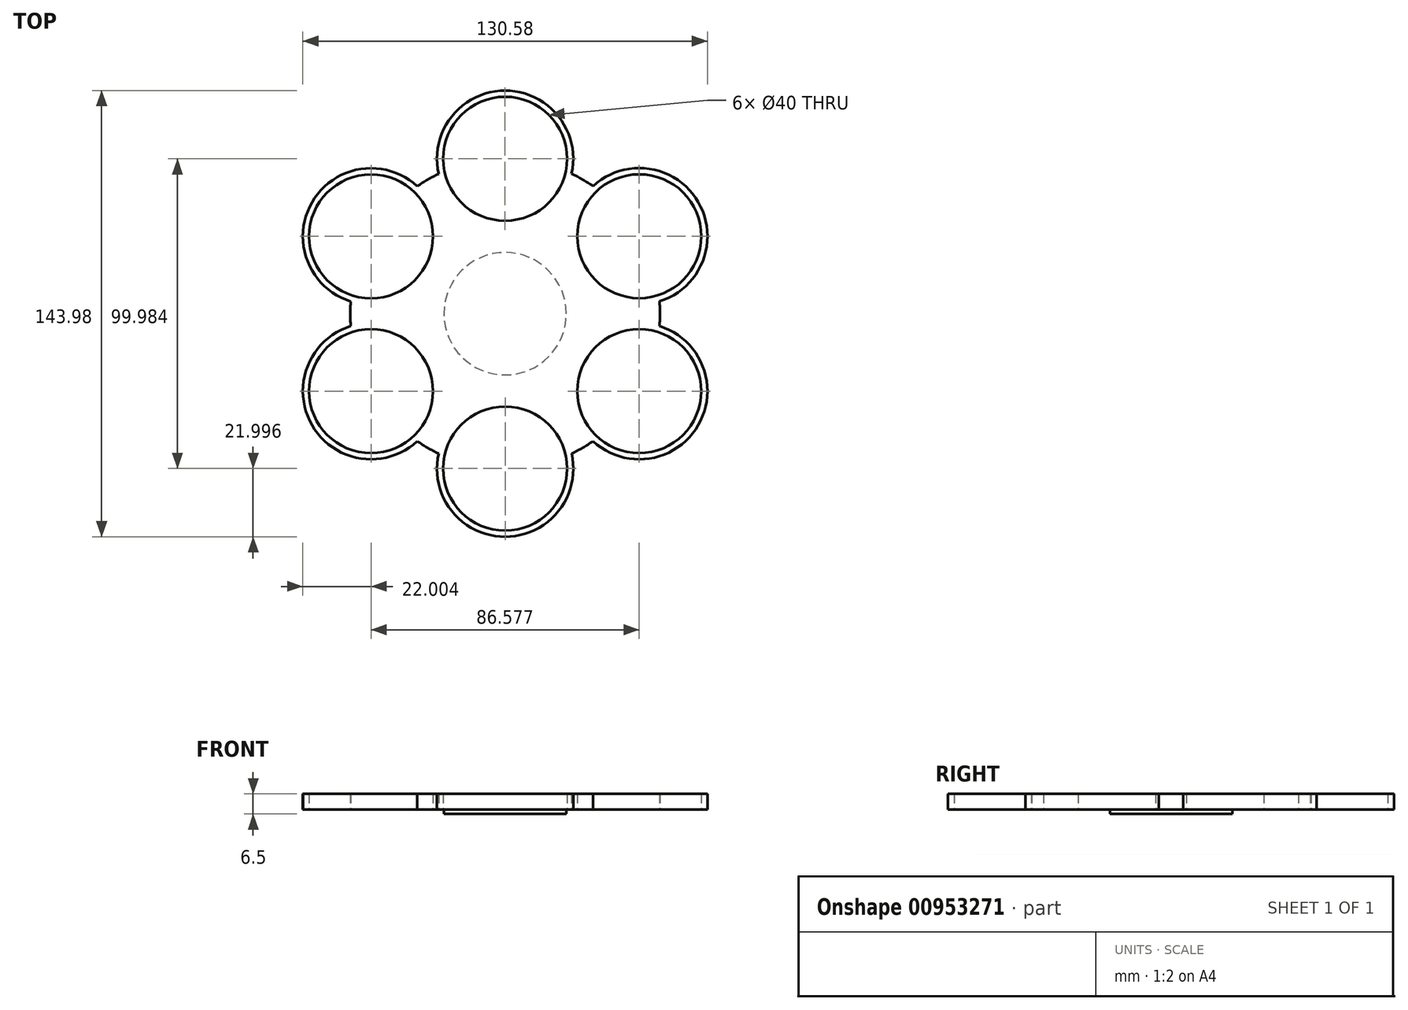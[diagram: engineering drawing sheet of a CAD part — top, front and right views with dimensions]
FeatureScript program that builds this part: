
annotation { "Feature Type Name" : "Feature", "Feature Type Description" : "" }
export const myFeature = defineFeature(function(context is Context, id is Id, definition is map)
    precondition{}
    {
        {
            var Q0;
            Q0=qCreatedBy(makeId("Top.planeOp"),FACE);
            var sketch = newSketch(context, id + "F0", { "sketchPlane" : qUnion([Q0])});
            skCircle(sketch, "E0", {"center": v(0, 0) * mm, "radius": 19.75 * mm});
            skSolve(sketch);
        }
        {
            var Q0;
            Q0=makeQuery(id+"F0.imprint","IMPRINT",FACE,{"disambiguationData":[TD([[makeQuery(id+"F0.imprint","IMPRINT",EDGE,{"derivedFrom":sQuery(id+"F0.wireOp",EDGE,"E0")}),1.0]])]});
            extrude(context, id + "F1", {"entities" : qUnion([Q0]), "depth" : 1.5 * mm, "offsetDistance" : 25 * mm});
        }
        {
            var Q0;
            Q0=makeQuery(id+"F1.opExtrude","CAP_FACE",FACE,{"disambiguationData":[OSD([sQuery(id+"F0.wireOp",EDGE,"E0")])],"isStart":false});
            var sketch = newSketch(context, id + "F2", { "sketchPlane" : qUnion([Q0])});
            skCircle(sketch, "E1", {"center": v(0, 50) * mm, "radius": 20 * mm});
            skCircle(sketch, "E2", {"center": v(43.3, 25) * mm, "radius": 20 * mm});
            skCircle(sketch, "E3", {"center": v(43.3, -25) * mm, "radius": 20 * mm});
            skCircle(sketch, "E4", {"center": v(0, -49.98) * mm, "radius": 20 * mm});
            skCircle(sketch, "E5", {"center": v(-43.27, -25) * mm, "radius": 20 * mm});
            skCircle(sketch, "E6", {"center": v(-43.28, 24.96) * mm, "radius": 20 * mm});
            skArc(sketch, "E7", {"start": v(-28.35, 41.13) * mm, "mid": v(-62.33, 35.96) * mm, "end": v(-49.81, 3.96) * mm});
            skArc(sketch, "E8", {"start": v(-49.81, -4) * mm, "mid": v(-62.33, -36) * mm, "end": v(-28.35, -41.16) * mm});
            skArc(sketch, "E9", {"start": v(-49.81, -4) * mm, "mid": v(-49.97, -0.02) * mm, "end": v(-49.81, 3.96) * mm});
            skArc(sketch, "E10", {"start": v(-21.45, -45.14) * mm, "mid": v(0, -71.98) * mm, "end": v(21.47, -45.14) * mm});
            skArc(sketch, "E11", {"start": v(28.37, -41.16) * mm, "mid": v(62.35, -36) * mm, "end": v(49.83, -3.98) * mm});
            skArc(sketch, "E12", {"start": v(49.83, 4) * mm, "mid": v(62.36, 36) * mm, "end": v(28.38, 41.17) * mm});
            skArc(sketch, "E13", {"start": v(21.46, 45.16) * mm, "mid": v(-0.02, 72) * mm, "end": v(-21.45, 45.11) * mm});
            skArc(sketch, "E14", {"start": v(28.37, -41.16) * mm, "mid": v(25, -43.29) * mm, "end": v(21.47, -45.14) * mm});
            skArc(sketch, "E15", {"start": v(49.83, -3.98) * mm, "mid": v(50, 0) * mm, "end": v(49.83, 4) * mm});
            skArc(sketch, "E16", {"start": v(28.38, 41.17) * mm, "mid": v(25, 43.3) * mm, "end": v(21.46, 45.16) * mm});
            skArc(sketch, "E17", {"start": v(-21.45, 45.11) * mm, "mid": v(-24.98, 43.26) * mm, "end": v(-28.35, 41.13) * mm});
            skArc(sketch, "E18", {"start": v(-21.45, -45.14) * mm, "mid": v(-24.98, -43.3) * mm, "end": v(-28.35, -41.16) * mm});
            skSolve(sketch);
        }
        {
            var Q0;
            Q0=makeQuery(id+"F2.imprint","IMPRINT",FACE,{"disambiguationData":[TD([[makeQuery(id+"F2.imprint","IMPRINT",EDGE,{"derivedFrom":sQuery(id+"F2.wireOp",EDGE,"E1")}),-1.0]])]});
            var Q1;
            Q1=makeQuery(id+"F2.imprint","IMPRINT",FACE,{"disambiguationData":[TD([[makeQuery(id+"F2.imprint","IMPRINT",EDGE,{"derivedFrom":makeQuery(id+"F1.opExtrude","CAP_EDGE",EDGE,{"disambiguationData":[OSD([sQuery(id+"F0.wireOp",EDGE,"E0")])],"isStart":false})}),1.0]])]});
            extrude(context, id + "F3", {"entities" : qUnion([Q0, Q1]), "operationType" : NewBodyOperationType.ADD, "depth" : 5 * mm, "offsetDistance" : 25 * mm});
        }
    });
